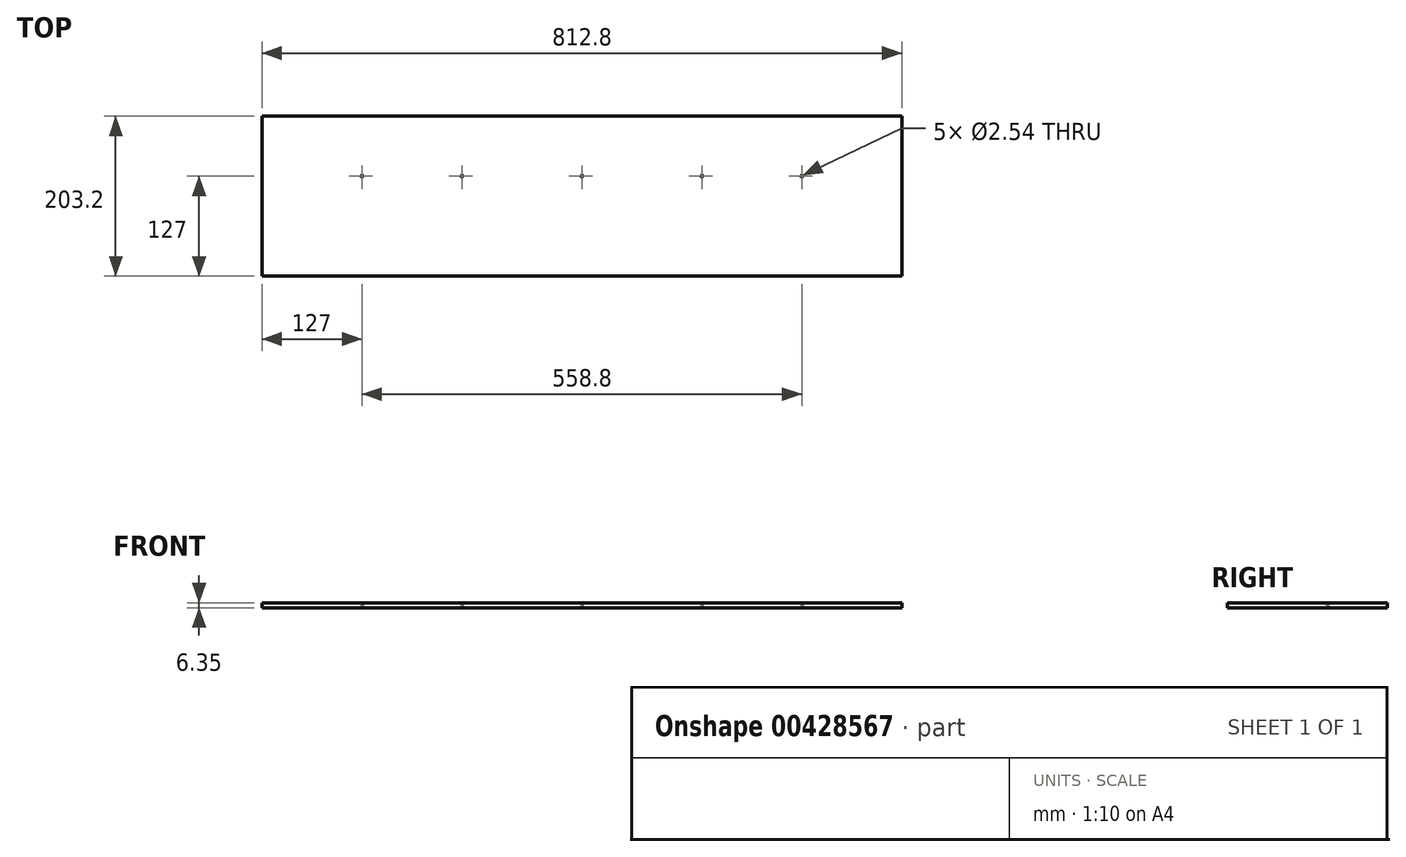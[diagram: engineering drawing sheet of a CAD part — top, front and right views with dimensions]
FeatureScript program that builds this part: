
annotation { "Feature Type Name" : "Feature", "Feature Type Description" : "" }
export const myFeature = defineFeature(function(context is Context, id is Id, definition is map)
    precondition{}
    {
        {
            var Q0;
            Q0=qCreatedBy(makeId("Top.planeOp"),FACE);
            var sketch = newSketch(context, id + "F0", { "sketchPlane" : qUnion([Q0])});
            skLineSegment(sketch, "E0.bottom", {"start": v(-457.2, -127) * mm, "end": v(457.2, -127) * mm});
            skLineSegment(sketch, "E0.top", {"start": v(-457.2, 127) * mm, "end": v(457.2, 127) * mm});
            skLineSegment(sketch, "E0.left", {"start": v(-457.2, -127) * mm, "end": v(-457.2, 127) * mm});
            skLineSegment(sketch, "E0.right", {"start": v(457.2, -127) * mm, "end": v(457.2, 127) * mm});
            skPoint(sketch, "E0.middle", {"position": v(0, 0) * mm});
            skLineSegment(sketch, "E1.bottom", {"start": v(-457.2, 127) * mm, "end": v(-406.4, 127) * mm});
            skLineSegment(sketch, "E1.top", {"start": v(-457.2, -127) * mm, "end": v(-406.4, -127) * mm});
            skLineSegment(sketch, "E1.left", {"start": v(-457.2, 127) * mm, "end": v(-457.2, -127) * mm});
            skLineSegment(sketch, "E1.right", {"start": v(-406.4, 127) * mm, "end": v(-406.4, -127) * mm});
            skLineSegment(sketch, "E2.bottom", {"start": v(457.2, 127) * mm, "end": v(406.4, 127) * mm});
            skLineSegment(sketch, "E2.top", {"start": v(457.2, -127) * mm, "end": v(406.4, -127) * mm});
            skLineSegment(sketch, "E2.left", {"start": v(457.2, 127) * mm, "end": v(457.2, -127) * mm});
            skLineSegment(sketch, "E2.right", {"start": v(406.4, 127) * mm, "end": v(406.4, -127) * mm});
            skCircle(sketch, "E3", {"center": v(431.8, -50.8) * mm, "radius": 1.27 * mm});
            skCircle(sketch, "E4", {"center": v(431.8, 50.8) * mm, "radius": 1.27 * mm});
            skCircle(sketch, "E5", {"center": v(-431.8, 50.8) * mm, "radius": 1.27 * mm});
            skCircle(sketch, "E6", {"center": v(-431.8, -50.8) * mm, "radius": 1.27 * mm});
            skLineSegment(sketch, "E7.bottom", {"start": v(406.4, 127) * mm, "end": v(-406.4, 127) * mm});
            skLineSegment(sketch, "E7.top", {"start": v(406.4, 76.2) * mm, "end": v(-406.4, 76.2) * mm});
            skLineSegment(sketch, "E7.left", {"start": v(406.4, 127) * mm, "end": v(406.4, 76.2) * mm});
            skLineSegment(sketch, "E7.right", {"start": v(-406.4, 127) * mm, "end": v(-406.4, 76.2) * mm});
            skCircle(sketch, "E8", {"center": v(-279.4, 0) * mm, "radius": 1.27 * mm});
            skCircle(sketch, "E9", {"center": v(-152.4, 0) * mm, "radius": 1.27 * mm});
            skCircle(sketch, "E10", {"center": v(152.4, 0) * mm, "radius": 1.27 * mm});
            skCircle(sketch, "E11", {"center": v(279.4, 0) * mm, "radius": 1.27 * mm});
            skCircle(sketch, "E12", {"center": v(0, 0) * mm, "radius": 1.27 * mm});
            skLineSegment(sketch, "E13.bottom", {"start": v(-406.4, -25.4) * mm, "end": v(406.4, -25.4) * mm});
            skLineSegment(sketch, "E13.top", {"start": v(-406.4, 25.4) * mm, "end": v(406.4, 25.4) * mm});
            skLineSegment(sketch, "E13.left", {"start": v(-406.4, -25.4) * mm, "end": v(-406.4, 25.4) * mm});
            skLineSegment(sketch, "E13.right", {"start": v(406.4, -25.4) * mm, "end": v(406.4, 25.4) * mm});
            skLineSegment(sketch, "E14.bottom", {"start": v(-482.6, 127) * mm, "end": v(-381, 127) * mm});
            skLineSegment(sketch, "E14.top", {"start": v(-482.6, 177.8) * mm, "end": v(-381, 177.8) * mm});
            skLineSegment(sketch, "E14.left", {"start": v(-482.6, 127) * mm, "end": v(-482.6, 177.8) * mm});
            skLineSegment(sketch, "E14.right", {"start": v(-381, 127) * mm, "end": v(-381, 177.8) * mm});
            skLineSegment(sketch, "E15.bottom", {"start": v(381, 127) * mm, "end": v(482.6, 127) * mm});
            skLineSegment(sketch, "E15.top", {"start": v(381, 177.8) * mm, "end": v(482.6, 177.8) * mm});
            skLineSegment(sketch, "E15.left", {"start": v(381, 127) * mm, "end": v(381, 177.8) * mm});
            skLineSegment(sketch, "E15.right", {"start": v(482.6, 127) * mm, "end": v(482.6, 177.8) * mm});
            skLineSegment(sketch, "E16.bottom", {"start": v(482.6, -177.8) * mm, "end": v(381, -177.8) * mm});
            skLineSegment(sketch, "E16.top", {"start": v(482.6, -127) * mm, "end": v(381, -127) * mm});
            skLineSegment(sketch, "E16.left", {"start": v(482.6, -177.8) * mm, "end": v(482.6, -127) * mm});
            skLineSegment(sketch, "E16.right", {"start": v(381, -177.8) * mm, "end": v(381, -127) * mm});
            skLineSegment(sketch, "E17.bottom", {"start": v(-381, -177.8) * mm, "end": v(-482.6, -177.8) * mm});
            skLineSegment(sketch, "E17.top", {"start": v(-381, -127) * mm, "end": v(-482.6, -127) * mm});
            skLineSegment(sketch, "E17.left", {"start": v(-381, -177.8) * mm, "end": v(-381, -127) * mm});
            skLineSegment(sketch, "E17.right", {"start": v(-482.6, -177.8) * mm, "end": v(-482.6, -127) * mm});
            skSolve(sketch);
        }
        {
            var Q0;
            Q0=makeQuery(id+"F0.imprint","IMPRINT",FACE,{"disambiguationData":[TD([[makeQuery(id+"F0.imprint","IMPRINT",EDGE,{"derivedFrom":sQuery(id+"F0.wireOp",EDGE,"E0.bottom")}),1.0]])]});
            var Q1;
            Q1=makeQuery(id+"F0.imprint","IMPRINT",FACE,{"disambiguationData":[TD([[makeQuery(id+"F0.imprint","IMPRINT",EDGE,{"derivedFrom":sQuery(id+"F0.wireOp",EDGE,"E1.bottom")}),-1.0]])]});
            var Q2;
            Q2=makeQuery(id+"F0.imprint","IMPRINT",FACE,{"disambiguationData":[TD([[makeQuery(id+"F0.imprint","IMPRINT",EDGE,{"derivedFrom":sQuery(id+"F0.wireOp",EDGE,"E7.bottom")}),1.0]])]});
            var Q3;
            Q3=makeQuery(id+"F0.imprint","IMPRINT",FACE,{"disambiguationData":[TD([[makeQuery(id+"F0.imprint","IMPRINT",EDGE,{"derivedFrom":sQuery(id+"F0.wireOp",EDGE,"E2.bottom")}),1.0]])]});
            var Q4;
            {var subQ0=sQuery(id+"F0.wireOp",EDGE,"E7.top");Q4=makeQuery(id+"F0.imprint","IMPRINT",FACE,{"disambiguationData":[TD([[makeQuery(id+"F0.imprint","IMPRINT",EDGE,{"derivedFrom":subQ0}),1.0]])]});}
            var Q5;
            Q5=makeQuery(id+"F0.imprint","IMPRINT",FACE,{"disambiguationData":[TD([[makeQuery(id+"F0.imprint","IMPRINT",EDGE,{"derivedFrom":sQuery(id+"F0.wireOp",EDGE,"E8")}),-1.0]])]});
            var Q6;
            {var subQ6=sQuery(id+"F0.wireOp",EDGE,"E1.left");Q6=makeQuery(id+"F0.imprint","IMPRINT",FACE,{"disambiguationData":[TD([[makeQuery(id+"F0.imprint","IMPRINT",EDGE,{"derivedFrom":subQ6}),1.0]])]});}
            var Q7;
            {var subQ5=sQuery(id+"F0.wireOp",EDGE,"E2.left");Q7=makeQuery(id+"F0.imprint","IMPRINT",FACE,{"disambiguationData":[TD([[makeQuery(id+"F0.imprint","IMPRINT",EDGE,{"derivedFrom":subQ5}),-1.0]])]});}
            extrude(context, id + "F1", {"entities" : qUnion([Q0, Q1, Q2, Q3, Q4, Q5, Q6, Q7]), "depth" : 6.35 * mm});
        }
    });
